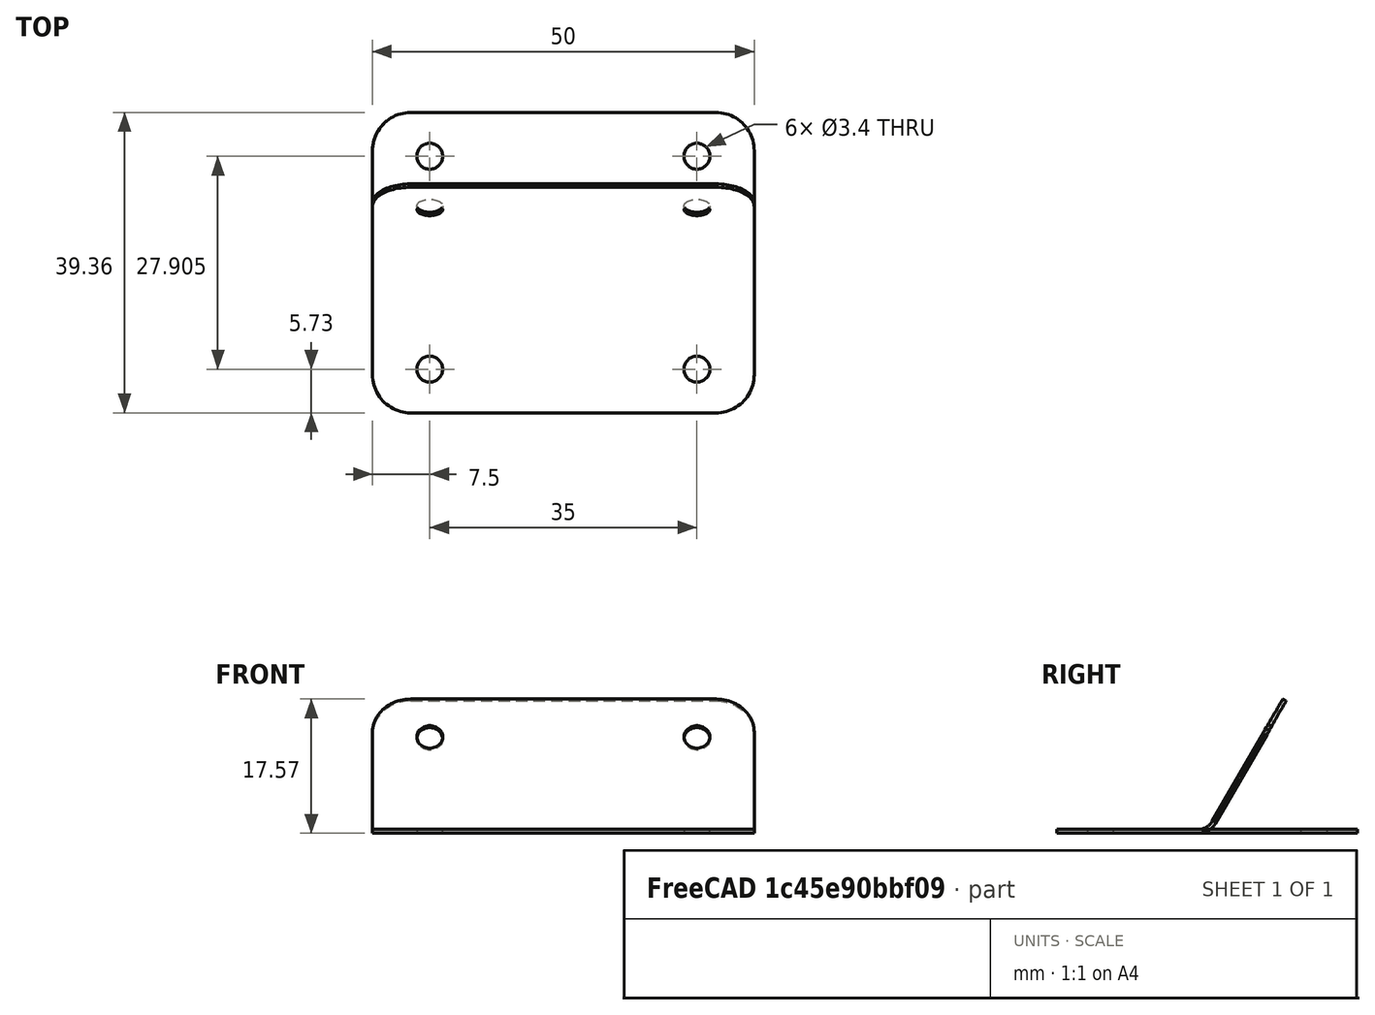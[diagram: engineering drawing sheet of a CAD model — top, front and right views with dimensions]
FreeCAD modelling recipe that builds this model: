
FCSTD DOCUMENT  (FreeCAD 0.21R31917 (Git))
Label: ugol120degX35mm
License: All rights reserved
LicenseURL: http://en.wikipedia.org/wiki/All_rights_reserved
objects: Sketcher::SketchObject×5, TechDraw::DrawViewDimension×5, PartDesign::SubShapeBinder×3, PartDesign::Pocket×2, TechDraw::DrawViewPart×2, PartDesign::FeaturePython×1, PartDesign::Fillet×1, PartDesign::Body×1, Part::Feature×1, TechDraw::DrawSVGTemplate×1, TechDraw::DrawPage×1
note: 17 computed .brp shape members not serialized (recipe doc carries the construction recipe); baked Part::Feature solids carry a one-line shape summary decoded from their .brp

FEATURE [Sketcher::SketchObject] Sketch
  FullyConstrained = true
  MapMode = 5
  Placement = pos=(0,0,0) rot=(0.57735,0.57735,0.57735;2.0944rad)
  Support = -> [YZ_Plane]
  sketch-geometry (2):
    g0: LineSegment StartX=-20 StartY=0 StartZ=0 EndX=0 EndY=0 EndZ=0
    g1: LineSegment StartX=0 StartY=0 StartZ=0 EndX=10 EndY=17.3205 EndZ=0
  constraints (6):
    c: PointOnObject(g0,g-1)
    c: Coincident(g0,g-1)
    c: Coincident(g0,g1)
    c: Angle(g1,g0) = 2.0944
    c: Equal(g0,g1)
    c: Distance(g0) = 20
FEATURE [PartDesign::FeaturePython] BaseBend  # WARN: FeaturePython — macro-defined, semantics opaque (R4)
  BendSide = 1
  BendSketch = -> Sketch
  MidPlane = true
  Reverse = false
  length = 50
  radius = 2
  thickness = 0.5
FEATURE [Sketcher::SketchObject] Sketch001
  AttachmentOffset = pos=(0,-14.27,0) rot=(0,0,1;0rad)
  FullyConstrained = true
  MapMode = 5
  Placement = pos=(0,-14.27,0) rot=(0,0,1;0rad)
  Support = -> [XY_Plane]
  expr: Constraints[2] = 3.4mm
  sketch-geometry (2):
    g0: Circle CenterX=17.5 CenterY=0 CenterZ=0 NormalX=0 NormalY=0 NormalZ=1 AngleXU=0 Radius=1.7
    g1: Circle CenterX=-17.5 CenterY=0 CenterZ=0 NormalX=0 NormalY=0 NormalZ=1 AngleXU=0 Radius=1.7
  constraints (5):
    c: PointOnObject(g0,g-1)
    c: Equal(g1,g0)
    c: Diameter(g1) = 3.4
    c: Symmetric(g0,g1,g-2)
    c: DistanceX(g1,g0) = 35
FEATURE [PartDesign::SubShapeBinder] Binder
  BindCopyOnChange = 0
  BindMode = 0
  ClaimChildren = false
  Context = -> Body [Binder.]
  Fuse = false
  MakeFace = true
  OffsetFill = false
  OffsetIntersection = false
  OffsetJoinType = 0
  OffsetOpenResult = false
  PartialLoad = false
  Placement = pos=(0,0,0) rot=(1,0,0;4.18879rad)
  Relative = false
  _Version = 2
FEATURE [PartDesign::Fillet] Fillet
  Base = -> BaseBend [Edge23,Edge25,Edge10,Edge8]
  BaseFeature = -> BaseBend
  Radius = 5
  SupportTransform = false
  UseAllEdges = false
FEATURE [PartDesign::SubShapeBinder] Binder001
  BindCopyOnChange = 0
  BindMode = 0
  ClaimChildren = false
  Context = -> Body [Binder001.]
  Fuse = false
  MakeFace = true
  OffsetFill = false
  OffsetIntersection = false
  OffsetJoinType = 0
  OffsetOpenResult = false
  PartialLoad = false
  Relative = true
  Support = -> [Sketch001]
  _Version = 2
FEATURE [PartDesign::Pocket] Pocket
  BaseFeature = -> Fillet
  Direction = (0,0,-1)
  Length = 5
  Length2 = 5
  Midplane = true
  Profile = -> Binder001
  Type = 1
FEATURE [PartDesign::SubShapeBinder] Binder002
  BindCopyOnChange = 0
  BindMode = 0
  ClaimChildren = false
  Context = -> Body [Binder002.]
  Fuse = false
  MakeFace = true
  OffsetFill = false
  OffsetIntersection = false
  OffsetJoinType = 0
  OffsetOpenResult = false
  PartialLoad = false
  Relative = true
  Support = -> [Binder]
  _Version = 2
FEATURE [PartDesign::Pocket] Pocket001
  BaseFeature = -> Pocket
  Direction = (0,-0.866025,0.5)
  Length = 5
  Length2 = 5
  Midplane = true
  Profile = -> Binder002
  Type = 1
FEATURE [PartDesign::Body] Body  label="Body_material_0.30ansi"
  Group = -> [Sketch,BaseBend,Sketch001,Fillet,Binder001,Binder,Pocket,Pocket001,Binder002]
  Origin = -> Origin
  Tip = -> Pocket001
FEATURE [Part::Feature] Unfold
  shape: bbox 50 x 39.37 x 0.5632 mm, 14 faces (baked)
FEATURE [Sketcher::SketchObject] Unfold_Sketch
  FullyConstrained = false
  sketch-geometry (12):
    g0: LineSegment StartX=-20 StartY=19.3647 StartZ=0 EndX=20 EndY=19.3647 EndZ=0
    g1: BSplineCurve PolesCount=22 KnotsCount=5 Degree=6 IsPeriodic=0
    g2: BSplineCurve PolesCount=22 KnotsCount=5 Degree=6 IsPeriodic=0
    g3: LineSegment StartX=-25 StartY=-15 StartZ=0 EndX=-25 EndY=14.3647 EndZ=0
    g4: BSplineCurve PolesCount=22 KnotsCount=5 Degree=6 IsPeriodic=0
    g5: LineSegment StartX=-20 StartY=-20 StartZ=0 EndX=20 EndY=-20 EndZ=0
    g6: BSplineCurve PolesCount=22 KnotsCount=5 Degree=6 IsPeriodic=0
    g7: LineSegment StartX=25 StartY=-15 StartZ=0 EndX=25 EndY=14.3647 EndZ=0
    g8: Circle CenterX=17.5 CenterY=13.6347 CenterZ=0 NormalX=0 NormalY=0 NormalZ=-1 AngleXU=-3.14159 Radius=1.7
    g9: Circle CenterX=-17.5 CenterY=13.6347 CenterZ=0 NormalX=0 NormalY=0 NormalZ=-1 AngleXU=-3.14159 Radius=1.7
    g10: Circle CenterX=17.5 CenterY=-14.27 CenterZ=0 NormalX=0 NormalY=0 NormalZ=1 AngleXU=0 Radius=1.7
    g11: Circle CenterX=-17.5 CenterY=-14.27 CenterZ=0 NormalX=0 NormalY=0 NormalZ=1 AngleXU=0 Radius=1.7
FEATURE [Sketcher::SketchObject] Unfold_Sketch_Outline
  FullyConstrained = false
  sketch-geometry (12):
    g0: BSplineCurve PolesCount=22 KnotsCount=5 Degree=6 IsPeriodic=0
    g1: LineSegment StartX=-20 StartY=19.3647 StartZ=0 EndX=20 EndY=19.3647 EndZ=0
    g2: BSplineCurve PolesCount=22 KnotsCount=5 Degree=6 IsPeriodic=0
    g3: LineSegment StartX=25 StartY=-15 StartZ=0 EndX=25 EndY=14.3647 EndZ=0
    g4: BSplineCurve PolesCount=22 KnotsCount=5 Degree=6 IsPeriodic=0
    g5: LineSegment StartX=-20 StartY=-20 StartZ=0 EndX=20 EndY=-20 EndZ=0
    g6: BSplineCurve PolesCount=22 KnotsCount=5 Degree=6 IsPeriodic=0
    g7: LineSegment StartX=-25 StartY=-15 StartZ=0 EndX=-25 EndY=14.3647 EndZ=0
    g8: Circle CenterX=17.5 CenterY=13.6347 CenterZ=0 NormalX=0 NormalY=0 NormalZ=-1 AngleXU=-3.14159 Radius=1.7
    g9: Circle CenterX=-17.5 CenterY=13.6347 CenterZ=0 NormalX=0 NormalY=0 NormalZ=-1 AngleXU=-3.14159 Radius=1.7
    g10: Circle CenterX=17.5 CenterY=-14.27 CenterZ=0 NormalX=0 NormalY=0 NormalZ=1 AngleXU=0 Radius=1.7
    g11: Circle CenterX=-17.5 CenterY=-14.27 CenterZ=0 NormalX=0 NormalY=0 NormalZ=1 AngleXU=0 Radius=1.7
FEATURE [Sketcher::SketchObject] Unfold_Sketch_bends
  FullyConstrained = false
  Placement = pos=(0,-0.00190285,0.0245111) rot=(1,0,0;0.077477rad)
  sketch-geometry (1):
    g0: LineSegment StartX=25 StartY=-0.316685 StartZ=0 EndX=-25 EndY=-0.316685 EndZ=0
FEATURE [TechDraw::DrawSVGTemplate] Template
  Height = 210
  Orientation = 1
  Template = <path>
  Width = 297
FEATURE [TechDraw::DrawViewPart] View
  CoarseView = false
  Direction = (1,0,0)
  Focus = 100
  HardHidden = false
  IsoCount = 0
  IsoHidden = false
  IsoVisible = false
  LockPosition = false
  Perspective = false
  Rotation = 0
  ScaleType = 0
  SeamHidden = false
  SeamVisible = true
  SmoothHidden = false
  SmoothVisible = true
  Source = -> [Body]
  X = 209.081
  XDirection = (0,1,-1.19209e-07)
  Y = 109.588
FEATURE [TechDraw::DrawViewPart] View001
  CoarseView = false
  Direction = (0,0,1)
  Focus = 100
  HardHidden = false
  IsoCount = 0
  IsoHidden = false
  IsoVisible = false
  LockPosition = false
  Perspective = false
  Rotation = 0
  ScaleType = 0
  SeamHidden = false
  SeamVisible = true
  SmoothHidden = false
  SmoothVisible = true
  Source = -> [Body]
  X = 113.428
  XDirection = (1,0,0)
  Y = 109.896
FEATURE [TechDraw::DrawViewDimension] Dimension
  AngleOverride = false
  Arbitrary = false
  ArbitraryTolerances = false
  EqualTolerance = true
  ExtensionAngle = 0
  FormatSpec = %.2w
  FormatSpecOverTolerance = %+.2w
  FormatSpecUnderTolerance = %+.2w
  Inverted = false
  LineAngle = 0
  LockPosition = false
  MeasureType = 1
  OverTolerance = 0
  References2D = -> [View]
  Rotation = 0
  ScaleType = 0
  TheoreticalExact = false
  Type = 0
  UnderTolerance = 0
  X = 10
  Y = 2.375
FEATURE [TechDraw::DrawViewDimension] Dimension001
  AngleOverride = false
  Arbitrary = false
  ArbitraryTolerances = false
  EqualTolerance = true
  ExtensionAngle = 0
  FormatSpec = %.2w
  FormatSpecOverTolerance = %+.2w
  FormatSpecUnderTolerance = %+.2w
  Inverted = false
  LineAngle = 0
  LockPosition = false
  MeasureType = 1
  OverTolerance = 0
  References2D = -> [View]
  Rotation = 0
  ScaleType = 0
  TheoreticalExact = false
  Type = 0
  UnderTolerance = 0
  X = -5
  Y = -6.28525
FEATURE [TechDraw::DrawViewDimension] Dimension002
  AngleOverride = false
  Arbitrary = false
  ArbitraryTolerances = false
  EqualTolerance = true
  ExtensionAngle = 0
  FormatSpec = %.2w
  FormatSpecOverTolerance = %+.2w
  FormatSpecUnderTolerance = %+.2w
  Inverted = false
  LineAngle = 0
  LockPosition = false
  MeasureType = 1
  OverTolerance = 0
  References2D = -> [View001]
  Rotation = 0
  ScaleType = 0
  TheoreticalExact = false
  Type = 0
  UnderTolerance = 0
  X = 6.04e-14
  Y = -6.77
FEATURE [TechDraw::DrawViewDimension] Dimension003
  AngleOverride = false
  Arbitrary = false
  ArbitraryTolerances = false
  EqualTolerance = true
  ExtensionAngle = 0
  FormatSpec = %.2w
  FormatSpecOverTolerance = %+.2w
  FormatSpecUnderTolerance = %+.2w
  Inverted = false
  LineAngle = 0
  LockPosition = false
  MeasureType = 1
  OverTolerance = 0
  References2D = -> [View001]
  Rotation = 0
  ScaleType = 0
  TheoreticalExact = false
  Type = 1
  UnderTolerance = 0
  X = -1.20166
  Y = -29.9933
FEATURE [TechDraw::DrawViewDimension] Dimension004
  AngleOverride = false
  Arbitrary = false
  ArbitraryTolerances = false
  EqualTolerance = true
  ExtensionAngle = 0
  FormatSpec = %.2w
  FormatSpecOverTolerance = %+.2w
  FormatSpecUnderTolerance = %+.2w
  Inverted = false
  LineAngle = 0
  LockPosition = false
  MeasureType = 1
  OverTolerance = 0
  References2D = -> [View]
  Rotation = 0
  ScaleType = 0
  TheoreticalExact = false
  Type = 6
  UnderTolerance = 0
  X = -7.81797
  Y = 11.1866
FEATURE [TechDraw::DrawPage] Page
  KeepUpdated = true
  NextBalloonIndex = 1
  ProjectionType = 0
  Template = -> Template
  Views = -> [View,View001,Dimension,Dimension001,Dimension002,Dimension003,Dimension004]
note: 1 file-system path scrubbed to <path> (originals preserved in the JSON sidecar)
